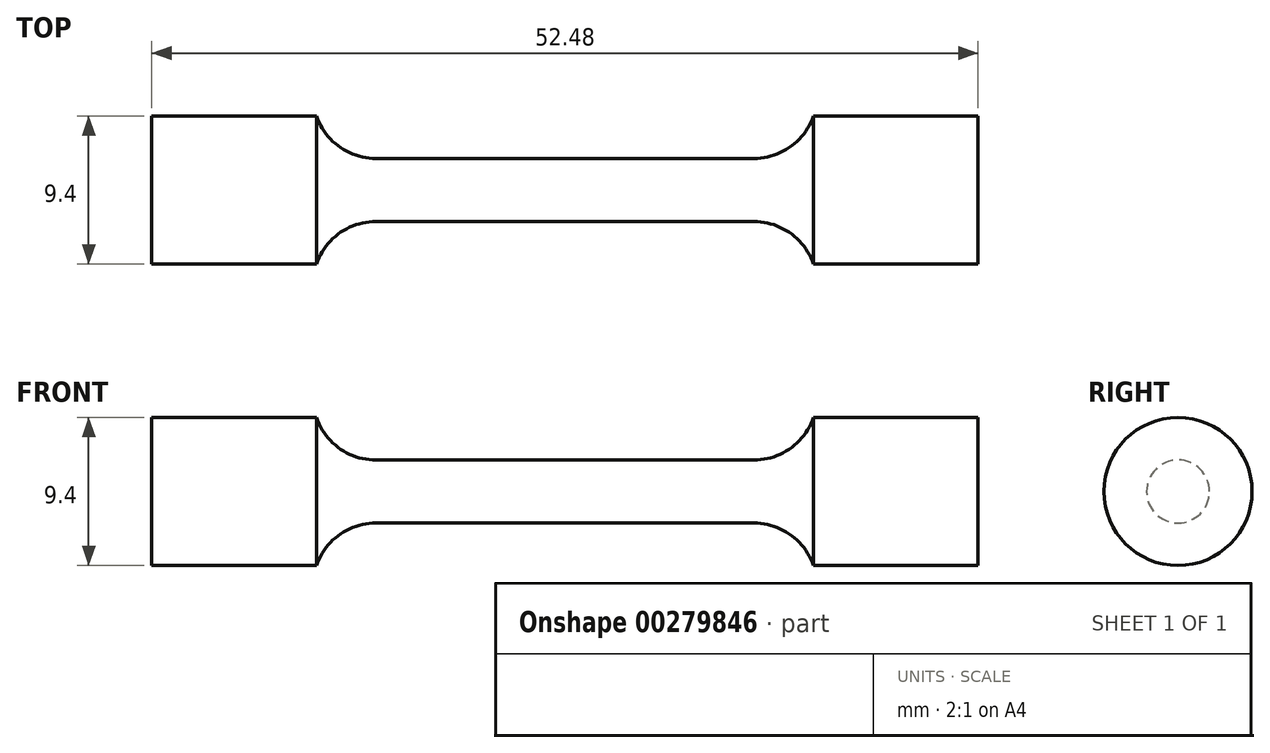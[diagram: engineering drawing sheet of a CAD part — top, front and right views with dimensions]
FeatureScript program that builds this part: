
annotation { "Feature Type Name" : "Feature", "Feature Type Description" : "" }
export const myFeature = defineFeature(function(context is Context, id is Id, definition is map)
    precondition{}
    {
        {
            var Q0;
            Q0=qCreatedBy(makeId("Front.planeOp"),FACE);
            var sketch = newSketch(context, id + "F0", { "sketchPlane" : qUnion([Q0])});
            skLineSegment(sketch, "E0", {"start": v(0, 2) * mm, "end": v(12, 2) * mm});
            skArc(sketch, "E1", {"start": v(12, 2) * mm, "mid": v(14.32, 2.75) * mm, "end": v(15.78, 4.7) * mm});
            skLineSegment(sketch, "E2", {"start": v(15.78, 4.7) * mm, "end": v(26.24, 4.7) * mm});
            skLineSegment(sketch, "E3", {"start": v(26.24, 4.7) * mm, "end": v(26.24, 0) * mm});
            skLineSegment(sketch, "E4.MirrorCS", {"start": v(0, 2) * mm, "end": v(-12, 2) * mm});
            skLineSegment(sketch, "E5.MirrorCS", {"start": v(-15.78, 4.7) * mm, "end": v(-26.24, 4.7) * mm});
            skArc(sketch, "E6.MirrorCS", {"start": v(-12, 2) * mm, "mid": v(-14.32, 2.75) * mm, "end": v(-15.78, 4.7) * mm});
            skLineSegment(sketch, "E7.MirrorCS", {"start": v(-26.24, 4.7) * mm, "end": v(-26.24, 0) * mm});
            skLineSegment(sketch, "E8", {"start": v(-26.24, 0) * mm, "end": v(26.24, 0) * mm});
            skSolve(sketch);
        }
        {
            var Q0;
            Q0=makeQuery(id+"F0.imprint","IMPRINT",FACE,{"disambiguationData":[TD([[makeQuery(id+"F0.imprint","IMPRINT",EDGE,{"derivedFrom":sQuery(id+"F0.wireOp",EDGE,"E0")}),-1.0]])]});
            var Q1;
            Q1=sQuery(id+"F0.wireOp",EDGE,"E8");
            revolve(context, id + "F1", {"entities" : qUnion([Q0]), "axis" : qUnion([Q1]), "revolveType" : RevolveType.FULL});
        }
    });
